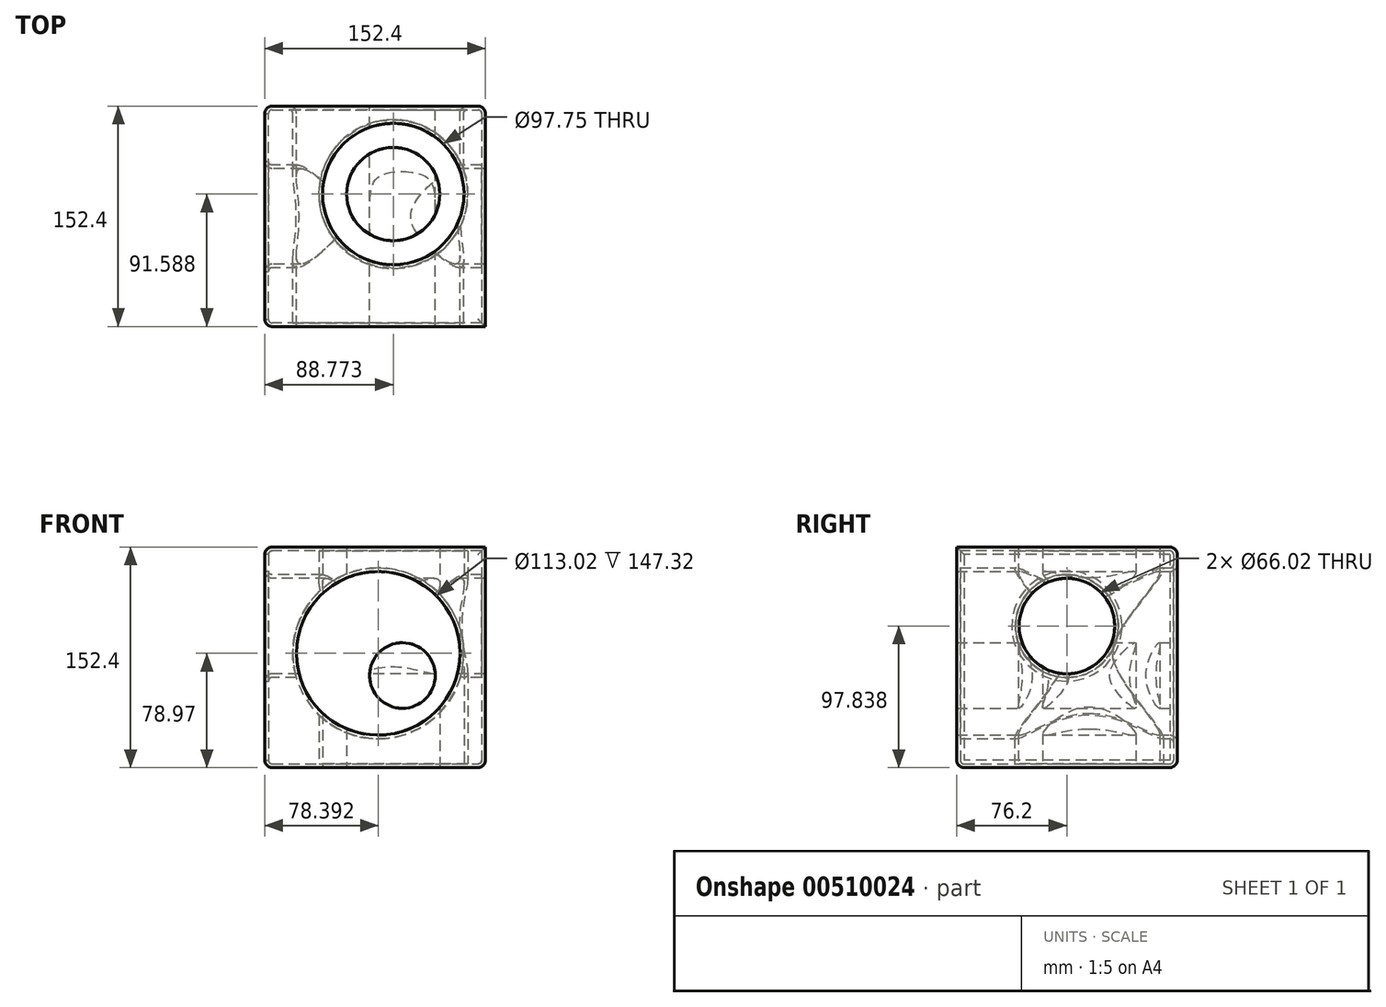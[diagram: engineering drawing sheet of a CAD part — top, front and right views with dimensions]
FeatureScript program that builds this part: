
annotation { "Feature Type Name" : "Feature", "Feature Type Description" : "" }
export const myFeature = defineFeature(function(context is Context, id is Id, definition is map)
    precondition{}
    {
        {
            var Q0;
            Q0=qCreatedBy(makeId("Top.planeOp"),FACE);
            var sketch = newSketch(context, id + "F0", { "sketchPlane" : qUnion([Q0])});
            skLineSegment(sketch, "E0.bottom", {"start": v(76.2, 76.2) * mm, "end": v(-76.2, 76.2) * mm});
            skLineSegment(sketch, "E0.top", {"start": v(76.2, -76.2) * mm, "end": v(-76.2, -76.2) * mm});
            skLineSegment(sketch, "E0.left", {"start": v(76.2, 76.2) * mm, "end": v(76.2, -76.2) * mm});
            skLineSegment(sketch, "E0.right", {"start": v(-76.2, 76.2) * mm, "end": v(-76.2, -76.2) * mm});
            skSolve(sketch);
        }
        {
            var Q0;
            Q0=makeQuery(id+"F0.imprint","IMPRINT",FACE,{"disambiguationData":[TD([[makeQuery(id+"F0.imprint","IMPRINT",EDGE,{"derivedFrom":sQuery(id+"F0.wireOp",EDGE,"E0.bottom")}),1.0]])]});
            extrude(context, id + "F1", {"entities" : qUnion([Q0]), "depth" : 152.4 * mm});
        }
        {
            var Q0;
            Q0=makeQuery(id+"F0.imprint","IMPRINT",FACE,{"disambiguationData":[TD([[makeQuery(id+"F0.imprint","IMPRINT",EDGE,{"derivedFrom":sQuery(id+"F0.wireOp",EDGE,"E0.bottom")}),1.0]])]});
            extrude(context, id + "F2", {"entities" : qUnion([Q0]), "operationType" : NewBodyOperationType.REMOVE, "oppositeDirection" : true, "depth" : 25.4 * mm});
        }
        {
            var Q0;
            Q0=makeQuery(id+"F1.opExtrude","SWEPT_FACE",FACE,{"disambiguationData":[OSD([sQuery(id+"F0.wireOp",EDGE,"E0.right")])]});
            var sketch = newSketch(context, id + "F3", { "sketchPlane" : qUnion([Q0])});
            skCircle(sketch, "E1", {"center": v(0, 97.84) * mm, "radius": 33 * mm});
            skSolve(sketch);
        }
        {
            var Q0;
            Q0=makeQuery(id+"F3.imprint","IMPRINT",FACE,{"disambiguationData":[TD([[makeQuery(id+"F3.imprint","IMPRINT",EDGE,{"derivedFrom":sQuery(id+"F3.wireOp",EDGE,"E1")}),1.0]])]});
            extrude(context, id + "F4", {"entities" : qUnion([Q0]), "operationType" : NewBodyOperationType.REMOVE, "oppositeDirection" : true, "depth" : 152.4 * mm});
        }
        {
            var Q0;
            Q0=makeQuery(id+"F1.opExtrude","SWEPT_FACE",FACE,{"disambiguationData":[OSD([sQuery(id+"F0.wireOp",EDGE,"E0.bottom")])]});
            var sketch = newSketch(context, id + "F5", { "sketchPlane" : qUnion([Q0])});
            skCircle(sketch, "E2", {"center": v(-18.9, 63.65) * mm, "radius": 22.67 * mm});
            skCircle(sketch, "E3", {"center": v(-2.2, 78.97) * mm, "radius": 56.51 * mm});
            skSolve(sketch);
        }
        {
            var Q0;
            Q0=makeQuery(id+"F5.imprint","IMPRINT",FACE,{"disambiguationData":[TD([[makeQuery(id+"F5.imprint","IMPRINT",EDGE,{"derivedFrom":sQuery(id+"F5.wireOp",EDGE,"E2")}),-1.0]])]});
            extrude(context, id + "F6", {"entities" : qUnion([Q0]), "operationType" : NewBodyOperationType.REMOVE, "oppositeDirection" : true, "depth" : 152.4 * mm});
        }
        {
            var Q0;
            Q0=makeQuery(id+"F1.opExtrude","CAP_FACE",FACE,{"disambiguationData":[OSD([sQuery(id+"F0.wireOp",EDGE,"E0.bottom"),sQuery(id+"F0.wireOp",EDGE,"E0.top"),sQuery(id+"F0.wireOp",EDGE,"E0.left"),sQuery(id+"F0.wireOp",EDGE,"E0.right")])],"isStart":true});
            var sketch = newSketch(context, id + "F7", { "sketchPlane" : qUnion([Q0])});
            skCircle(sketch, "E4", {"center": v(12.57, -15.39) * mm, "radius": 32.2 * mm});
            skCircle(sketch, "E5", {"center": v(12.57, -15.39) * mm, "radius": 48.88 * mm});
            skSolve(sketch);
        }
        {
            var Q0;
            Q0=makeQuery(id+"F7.imprint","IMPRINT",FACE,{"disambiguationData":[TD([[makeQuery(id+"F7.imprint","IMPRINT",EDGE,{"derivedFrom":sQuery(id+"F7.wireOp",EDGE,"E4")}),-1.0]])]});
            extrude(context, id + "F8", {"entities" : qUnion([Q0]), "operationType" : NewBodyOperationType.REMOVE, "oppositeDirection" : true, "depth" : 152.4 * mm});
        }
        {
            var Q0;
            {var subQ1=sQuery(id+"F0.wireOp",EDGE,"E0.left");var subQ3=sQuery(id+"F0.wireOp",EDGE,"E0.bottom");Q0=makeQuery(id+"F6.boolean.opBoolean","SPLIT",FACE,{"disambiguationData":[TD([makeQuery(id+"F1.opExtrude","SWEPT_FACE",FACE,{"disambiguationData":[OSD([subQ1])]})])],"derivedFrom":makeQuery(id+"F1.opExtrude","SWEPT_FACE",FACE,{"disambiguationData":[OSD([subQ3])]})});}
            var Q1;
            Q1=makeQuery(id+"F1.opExtrude","SWEPT_FACE",FACE,{"disambiguationData":[OSD([sQuery(id+"F0.wireOp",EDGE,"E0.right")])]});
            fillet(context, id + "F9", {"entities" : qUnion([Q0, Q1]), "radius" : 5.08 * mm, "tangentPropagation" : true, "allowEdgeOverflow" : false});
        }
        {
            var Q0;
            Q0=makeQuery(id+"F1.opExtrude","CAP_EDGE",EDGE,{"disambiguationData":[OSD([sQuery(id+"F0.wireOp",EDGE,"E0.left")])],"isStart":true});
            var Q1;
            Q1=makeQuery(id+"F1.opExtrude","CAP_EDGE",EDGE,{"disambiguationData":[OSD([sQuery(id+"F0.wireOp",EDGE,"E0.top")])],"isStart":true});
            var Q2;
            {var subQ1=sQuery(id+"F0.wireOp",EDGE,"E0.left");var subQ3=sQuery(id+"F0.wireOp",EDGE,"E0.bottom");Q2=makeQuery(id+"F9.opFillet","BLEND_EDGE",EDGE,{"blendedFrom":[makeQuery(id+"F1.opExtrude","SWEPT_EDGE",EDGE,{"disambiguationData":[OSD([subQ3,subQ1])]}),makeQuery(id+"F6.boolean.opBoolean","SPLIT",FACE,{"disambiguationData":[TD([makeQuery(id+"F1.opExtrude","SWEPT_FACE",FACE,{"disambiguationData":[OSD([subQ1])]})])],"derivedFrom":makeQuery(id+"F1.opExtrude","SWEPT_FACE",FACE,{"disambiguationData":[OSD([subQ3])]})})],"blendedInto":[makeQuery(id+"F6.boolean.opBoolean","SPLIT",FACE,{"disambiguationData":[TD([makeQuery(id+"F1.opExtrude","SWEPT_FACE",FACE,{"disambiguationData":[OSD([subQ1])]})])],"derivedFrom":makeQuery(id+"F1.opExtrude","SWEPT_FACE",FACE,{"disambiguationData":[OSD([subQ3])]})})]});}
            var Q3;
            {var subQ1=sQuery(id+"F0.wireOp",EDGE,"E0.left");var subQ3=sQuery(id+"F0.wireOp",EDGE,"E0.bottom");Q3=makeQuery(id+"F9.opFillet","BLEND_EDGE",EDGE,{"blendedFrom":[makeQuery(id+"F1.opExtrude","CAP_EDGE",EDGE,{"disambiguationData":[OSD([subQ3])],"isStart":false}),makeQuery(id+"F6.boolean.opBoolean","SPLIT",FACE,{"disambiguationData":[TD([makeQuery(id+"F1.opExtrude","SWEPT_FACE",FACE,{"disambiguationData":[OSD([subQ1])]})])],"derivedFrom":makeQuery(id+"F1.opExtrude","SWEPT_FACE",FACE,{"disambiguationData":[OSD([subQ3])]})})],"blendedInto":[makeQuery(id+"F6.boolean.opBoolean","SPLIT",FACE,{"disambiguationData":[TD([makeQuery(id+"F1.opExtrude","SWEPT_FACE",FACE,{"disambiguationData":[OSD([subQ1])]})])],"derivedFrom":makeQuery(id+"F1.opExtrude","SWEPT_FACE",FACE,{"disambiguationData":[OSD([subQ3])]})})]});}
            fillet(context, id + "F10", {"entities" : qUnion([Q0, Q1, Q2, Q3]), "radius" : 5.08 * mm, "tangentPropagation" : true, "allowEdgeOverflow" : false});
        }
        {
            var Q0;
            Q0=makeQuery(id+"F1.opExtrude","SWEPT_FACE",FACE,{"disambiguationData":[OSD([sQuery(id+"F0.wireOp",EDGE,"E0.right")])]});
            shell(context, id + "F11", {"entities" : qUnion([Q0]), "thickness" : 2.54 * mm});
        }
    });
